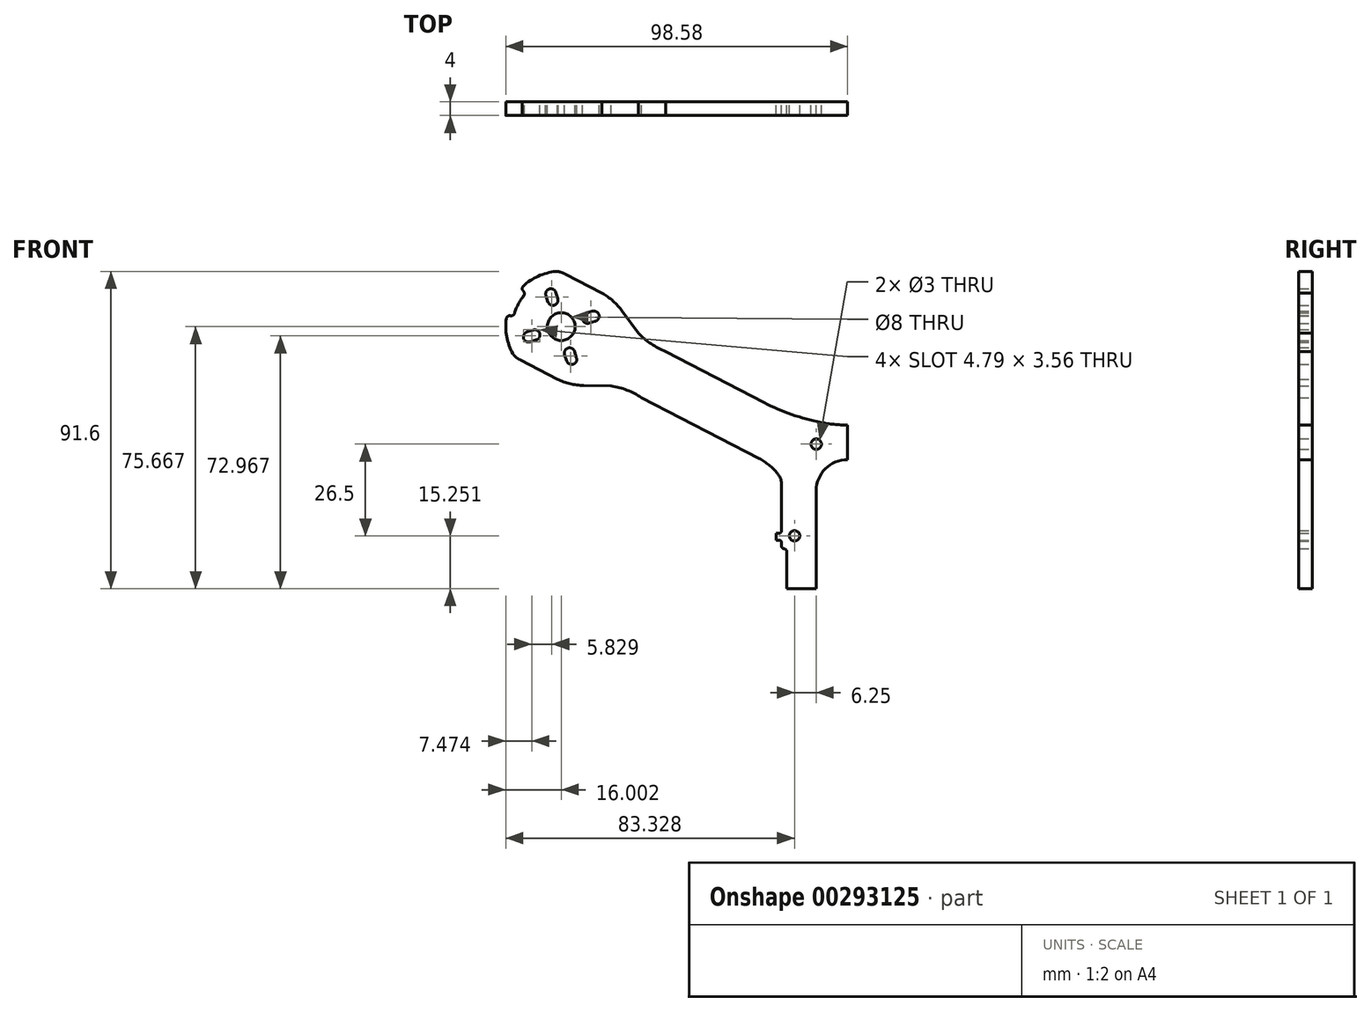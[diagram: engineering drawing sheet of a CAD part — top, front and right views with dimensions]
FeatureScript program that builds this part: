
annotation { "Feature Type Name" : "Feature", "Feature Type Description" : "" }
export const myFeature = defineFeature(function(context is Context, id is Id, definition is map)
    precondition{}
    {
        {
            var Q0;
            Q0=qCreatedBy(makeId("Front.planeOp"),FACE);
            var sketch = newSketch(context, id + "F0", { "sketchPlane" : qUnion([Q0])});
            skArc(sketch, "E0", {"start": v(-47.92, 33) * mm, "mid": v(-47.2, 33.12) * mm, "end": v(-46.75, 33.7) * mm});
            skArc(sketch, "E1", {"start": v(-44.13, 38.73) * mm, "mid": v(-45.7, 36.35) * mm, "end": v(-46.75, 33.7) * mm});
            skArc(sketch, "E2", {"start": v(-44.13, 38.73) * mm, "mid": v(-43.9, 39.43) * mm, "end": v(-44.22, 40.1) * mm});
            skArc(sketch, "E3", {"start": v(-44.22, 41.55) * mm, "mid": v(-44.54, 40.82) * mm, "end": v(-44.22, 40.1) * mm});
            skArc(sketch, "E4", {"start": v(-34.92, 45.78) * mm, "mid": v(-39.92, 44.43) * mm, "end": v(-44.22, 41.55) * mm});
            skArc(sketch, "E5", {"start": v(-33.83, 45.7) * mm, "mid": v(-34.37, 45.79) * mm, "end": v(-34.92, 45.78) * mm});
            skArc(sketch, "E6", {"start": v(-32.18, 45.07) * mm, "mid": v(-32.99, 45.42) * mm, "end": v(-33.83, 45.7) * mm});
            skArc(sketch, "E7", {"start": v(-32.14, 45.04) * mm, "mid": v(-32.16, 45.06) * mm, "end": v(-32.18, 45.07) * mm});
            skLineSegment(sketch, "E8", {"start": v(-32.14, 45.04) * mm, "end": v(-21.53, 39.54) * mm});
            skArc(sketch, "E9", {"start": v(-15.68, 34.36) * mm, "mid": v(-18.33, 37.26) * mm, "end": v(-21.53, 39.54) * mm});
            skLineSegment(sketch, "E10", {"start": v(-15.68, 34.36) * mm, "end": v(-11.04, 27.98) * mm});
            skArc(sketch, "E11", {"start": v(-11.04, 27.98) * mm, "mid": v(-7.38, 24.91) * mm, "end": v(-3.16, 22.68) * mm});
            skLineSegment(sketch, "E12", {"start": v(-3.16, 22.68) * mm, "end": v(25.29, 7.9) * mm});
            skArc(sketch, "E13", {"start": v(25.29, 7.9) * mm, "mid": v(33.22, 4.48) * mm, "end": v(41.56, 2.2) * mm});
            skArc(sketch, "E14", {"start": v(41.56, 2.2) * mm, "mid": v(45.4, 1.64) * mm, "end": v(49.29, 1.45) * mm});
            skLineSegment(sketch, "E15", {"start": v(49.29, 1.45) * mm, "end": v(49.29, -8.55) * mm});
            skArc(sketch, "E16", {"start": v(49.29, -8.55) * mm, "mid": v(42.92, -11.19) * mm, "end": v(40.29, -17.55) * mm});
            skLineSegment(sketch, "E17", {"start": v(40.29, -17.55) * mm, "end": v(40.29, -45.8) * mm});
            skLineSegment(sketch, "E18", {"start": v(40.29, -45.8) * mm, "end": v(31.79, -45.8) * mm});
            skLineSegment(sketch, "E19", {"start": v(31.79, -45.8) * mm, "end": v(31.79, -35.05) * mm});
            skArc(sketch, "E20", {"start": v(31.79, -35.05) * mm, "mid": v(31.57, -34.52) * mm, "end": v(31.04, -34.3) * mm});
            skArc(sketch, "E21", {"start": v(30.29, -33.55) * mm, "mid": v(30.5, -34.08) * mm, "end": v(31.04, -34.3) * mm});
            skLineSegment(sketch, "E22", {"start": v(30.29, -33.55) * mm, "end": v(30.29, -32.55) * mm});
            skArc(sketch, "E23", {"start": v(30.29, -32.55) * mm, "mid": v(30.07, -32.02) * mm, "end": v(29.54, -31.8) * mm});
            skLineSegment(sketch, "E24", {"start": v(29.54, -31.8) * mm, "end": v(28.79, -31.8) * mm});
            skLineSegment(sketch, "E25", {"start": v(28.79, -31.8) * mm, "end": v(28.79, -29.8) * mm});
            skLineSegment(sketch, "E26", {"start": v(28.79, -29.8) * mm, "end": v(29.54, -29.8) * mm});
            skArc(sketch, "E27", {"start": v(29.54, -29.8) * mm, "mid": v(30.07, -29.58) * mm, "end": v(30.29, -29.05) * mm});
            skLineSegment(sketch, "E28", {"start": v(30.29, -29.05) * mm, "end": v(30.29, -15.75) * mm});
            skArc(sketch, "E29", {"start": v(30.29, -15.75) * mm, "mid": v(30, -14.07) * mm, "end": v(29.16, -12.59) * mm});
            skArc(sketch, "E30", {"start": v(29.16, -12.59) * mm, "mid": v(26.67, -10.11) * mm, "end": v(23.74, -8.19) * mm});
            skLineSegment(sketch, "E31", {"start": v(23.74, -8.19) * mm, "end": v(-10.07, 9.37) * mm});
            skArc(sketch, "E32", {"start": v(-10.07, 9.37) * mm, "mid": v(-14.33, 11.53) * mm, "end": v(-18.94, 12.76) * mm});
            skLineSegment(sketch, "E33", {"start": v(-18.94, 12.76) * mm, "end": v(-26.83, 12.88) * mm});
            skArc(sketch, "E34", {"start": v(-34.43, 14.69) * mm, "mid": v(-30.72, 13.38) * mm, "end": v(-26.83, 12.88) * mm});
            skLineSegment(sketch, "E35", {"start": v(-34.43, 14.69) * mm, "end": v(-45.04, 20.2) * mm});
            skArc(sketch, "E36", {"start": v(-45.08, 20.22) * mm, "mid": v(-45.06, 20.2) * mm, "end": v(-45.04, 20.2) * mm});
            skArc(sketch, "E37", {"start": v(-46.54, 21.2) * mm, "mid": v(-45.84, 20.67) * mm, "end": v(-45.08, 20.22) * mm});
            skArc(sketch, "E38", {"start": v(-47.24, 22.04) * mm, "mid": v(-46.93, 21.59) * mm, "end": v(-46.54, 21.2) * mm});
            skArc(sketch, "E39", {"start": v(-49.12, 32.16) * mm, "mid": v(-49.02, 26.95) * mm, "end": v(-47.24, 22.04) * mm});
            skArc(sketch, "E40", {"start": v(-47.92, 33) * mm, "mid": v(-48.7, 32.84) * mm, "end": v(-49.12, 32.16) * mm});
            skLineSegment(sketch, "E41", {"start": v(-37.7, 38.84) * mm, "end": v(-37.13, 37.04) * mm});
            skArc(sketch, "E42", {"start": v(-34.84, 39.75) * mm, "mid": v(-36.73, 40.73) * mm, "end": v(-37.7, 38.84) * mm});
            skLineSegment(sketch, "E43", {"start": v(-34.27, 37.95) * mm, "end": v(-34.84, 39.75) * mm});
            skLineSegment(sketch, "E44", {"start": v(-28.87, 20.89) * mm, "end": v(-29.44, 22.7) * mm});
            skArc(sketch, "E45", {"start": v(-31.73, 19.98) * mm, "mid": v(-29.85, 19) * mm, "end": v(-28.87, 20.89) * mm});
            skLineSegment(sketch, "E46", {"start": v(-32.3, 21.79) * mm, "end": v(-31.73, 19.98) * mm});
            skCircle(sketch, "E47", {"center": v(34.04, -30.55) * mm, "radius": 1.5 * mm});
            skCircle(sketch, "E48", {"center": v(-33.29, 29.87) * mm, "radius": 4 * mm});
            skLineSegment(sketch, "E49", {"start": v(-42.26, 25.45) * mm, "end": v(-40.46, 26.02) * mm});
            skArc(sketch, "E50", {"start": v(-43.17, 28.31) * mm, "mid": v(-44.15, 26.43) * mm, "end": v(-42.26, 25.45) * mm});
            skLineSegment(sketch, "E51", {"start": v(-41.37, 28.88) * mm, "end": v(-43.17, 28.31) * mm});
            skLineSegment(sketch, "E52", {"start": v(-24.31, 34.28) * mm, "end": v(-26.11, 33.71) * mm});
            skArc(sketch, "E53", {"start": v(-23.4, 31.42) * mm, "mid": v(-22.43, 33.3) * mm, "end": v(-24.31, 34.28) * mm});
            skLineSegment(sketch, "E54", {"start": v(-25.2, 30.85) * mm, "end": v(-23.4, 31.42) * mm});
            skArc(sketch, "E55", {"start": v(-26.11, 33.71) * mm, "mid": v(-27.1, 31.83) * mm, "end": v(-25.2, 30.85) * mm});
            skArc(sketch, "E56", {"start": v(-40.46, 26.02) * mm, "mid": v(-39.48, 27.9) * mm, "end": v(-41.37, 28.88) * mm});
            skArc(sketch, "E57", {"start": v(-29.44, 22.7) * mm, "mid": v(-31.33, 23.67) * mm, "end": v(-32.3, 21.79) * mm});
            skArc(sketch, "E58", {"start": v(-37.13, 37.04) * mm, "mid": v(-35.25, 36.06) * mm, "end": v(-34.27, 37.95) * mm});
            skCircle(sketch, "E59", {"center": v(40.29, -4.05) * mm, "radius": 1.5 * mm});
            skSolve(sketch);
        }
        {
            var Q0;
            Q0=makeQuery(id+"F0.imprint","IMPRINT",FACE,{"disambiguationData":[TD([[makeQuery(id+"F0.imprint","IMPRINT",EDGE,{"derivedFrom":sQuery(id+"F0.wireOp",EDGE,"E0")}),-1.0]])]});
            extrude(context, id + "F1", {"entities" : qUnion([Q0]), "depth" : 4 * mm});
        }
    });
